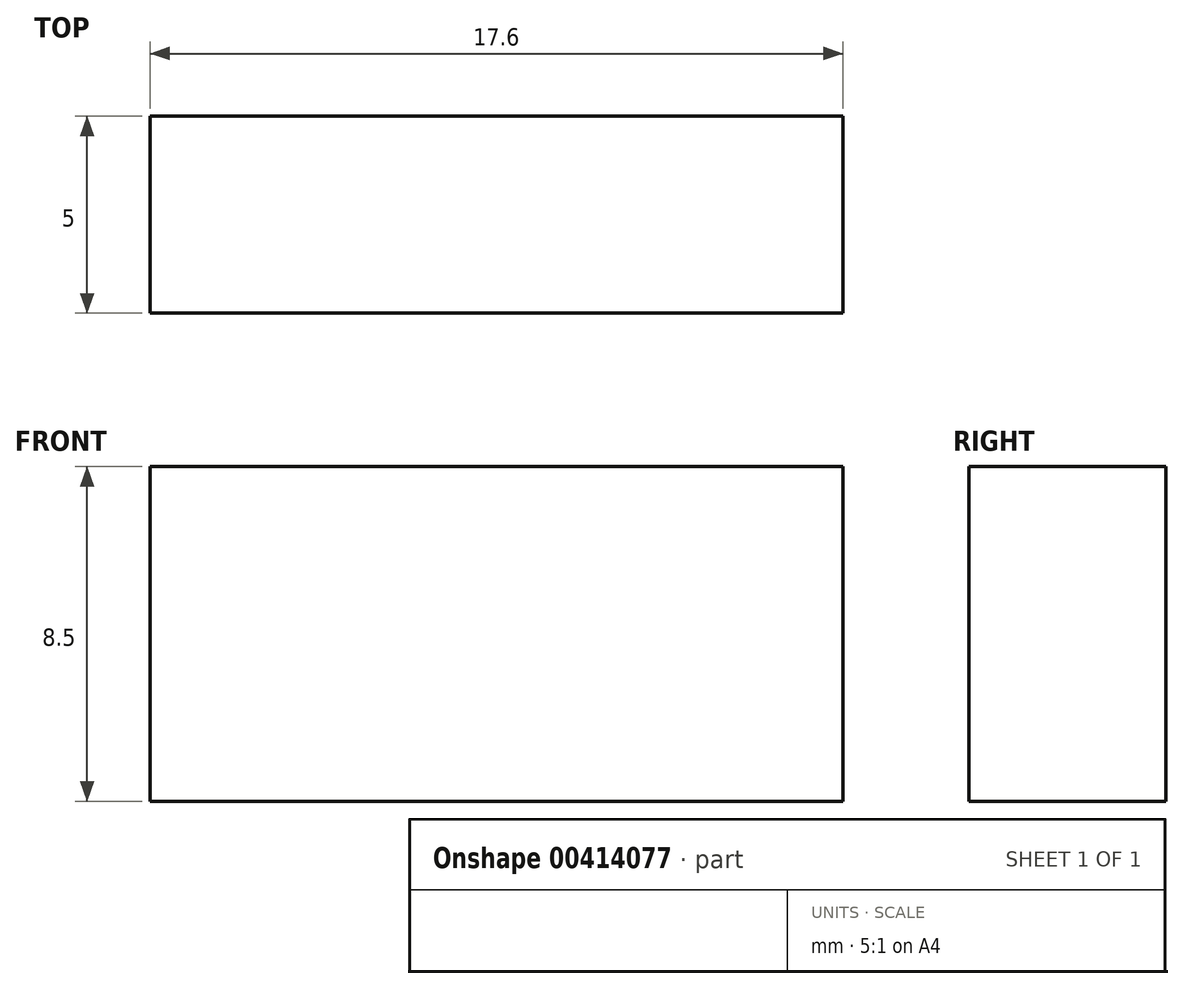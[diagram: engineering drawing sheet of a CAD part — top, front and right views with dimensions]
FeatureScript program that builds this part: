
annotation { "Feature Type Name" : "Feature", "Feature Type Description" : "" }
export const myFeature = defineFeature(function(context is Context, id is Id, definition is map)
    precondition{}
    {
        {
            var Q0;
            Q0=qCreatedBy(makeId("Front.planeOp"),FACE);
            var sketch = newSketch(context, id + "F0", { "sketchPlane" : qUnion([Q0])});
            skLineSegment(sketch, "E0.bottom", {"start": v(0, 0) * mm, "end": v(17.6, 0) * mm});
            skLineSegment(sketch, "E0.top", {"start": v(0, 8.5) * mm, "end": v(17.6, 8.5) * mm});
            skLineSegment(sketch, "E0.left", {"start": v(0, 0) * mm, "end": v(0, 8.5) * mm});
            skLineSegment(sketch, "E0.right", {"start": v(17.6, 0) * mm, "end": v(17.6, 8.5) * mm});
            skSolve(sketch);
        }
        {
            var Q0;
            Q0=makeQuery(id+"F0.imprint","IMPRINT",FACE,{"disambiguationData":[TD([[makeQuery(id+"F0.imprint","IMPRINT",EDGE,{"derivedFrom":sQuery(id+"F0.wireOp",EDGE,"E0.bottom")}),1.0]])]});
            extrude(context, id + "F1", {"entities" : qUnion([Q0]), "depth" : 5 * mm});
        }
    });
